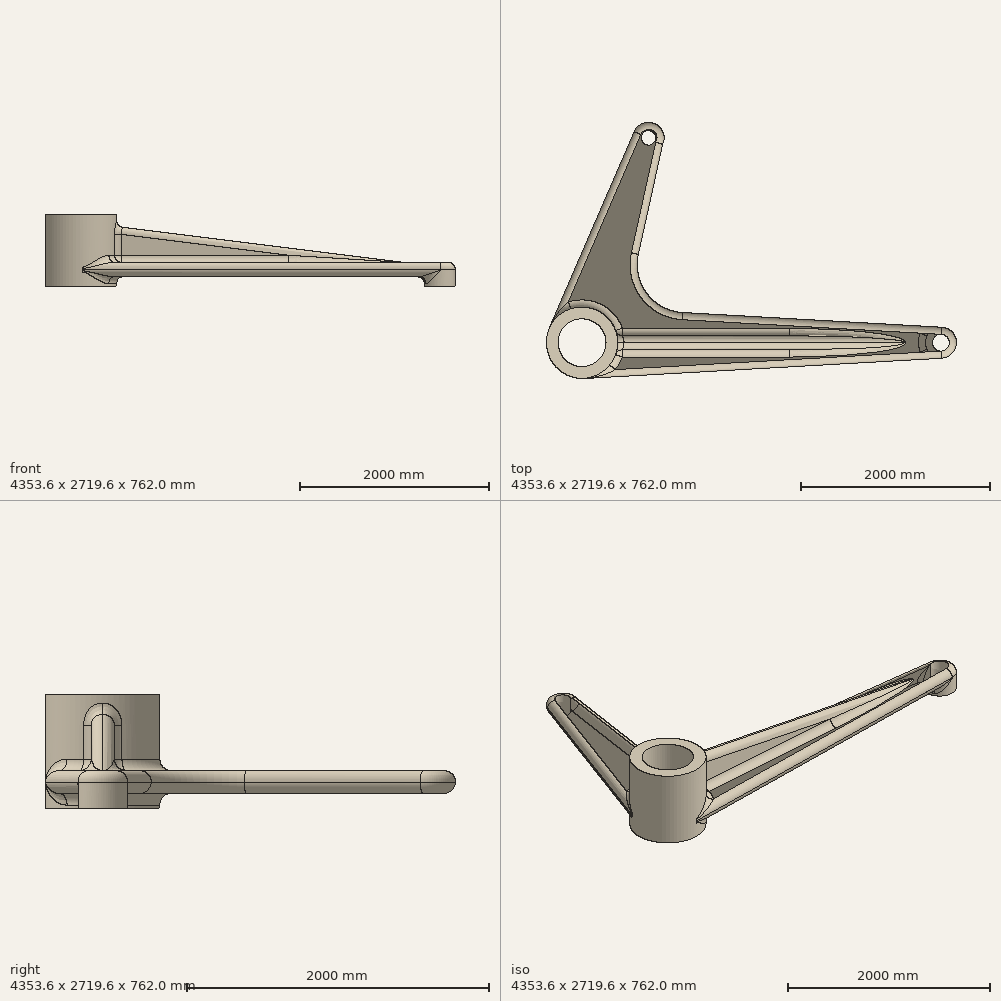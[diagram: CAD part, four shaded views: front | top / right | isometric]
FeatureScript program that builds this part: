
annotation { "Feature Type Name" : "Feature", "Feature Type Description" : "" }
export const myFeature = defineFeature(function(context is Context, id is Id, definition is map)
    precondition{}
    {
        {
            var Q0;
            Q0=qCreatedBy(makeId("Top.planeOp"),FACE);
            var sketch = newSketch(context, id + "F0", { "sketchPlane" : qUnion([Q0])});
            skArc(sketch, "E0", {"start": v(21.59, 380.39) * mm, "mid": v(-381, 0) * mm, "end": v(21.59, -380.39) * mm});
            skArc(sketch, "E1", {"start": v(3819.36, -164.83) * mm, "mid": v(3975.1, 0) * mm, "end": v(3819.36, 164.83) * mm});
            skLineSegment(sketch, "E2", {"start": v(3819.36, 164.83) * mm, "end": v(21.59, 380.39) * mm});
            skLineSegment(sketch, "E3", {"start": v(3819.36, -164.83) * mm, "end": v(21.59, -380.39) * mm});
            skSolve(sketch);
        }
        {
            var Q0;
            Q0 = qSketchRegion(id + "F0", true);
            extrude(context, id + "F1", {"entities" : qUnion([Q0]), "oppositeDirection" : true, "depth" : 152.4 * mm, "offsetDistance" : 25.4 * mm});
        }
        {
            var Q0;
            Q0=makeQuery(id+"F1.opExtrude","CAP_FACE",FACE,{"disambiguationData":[OSD([sQuery(id+"F0.wireOp",EDGE,"E0"),sQuery(id+"F0.wireOp",EDGE,"E1"),sQuery(id+"F0.wireOp",EDGE,"E2"),sQuery(id+"F0.wireOp",EDGE,"E3")])],"isStart":true});
            var sketch = newSketch(context, id + "F2", { "sketchPlane" : qUnion([Q0])});
            skLineSegment(sketch, "E4", {"start": v(0, 0) * mm, "end": v(706.41, 2174.12) * mm, "construction": true});
            skLineSegment(sketch, "E5", {"start": v(0, 0) * mm, "end": v(5447.22, 0) * mm, "construction": true});
            skArc(sketch, "E6", {"start": v(856.09, 2104.43) * mm, "mid": v(774.07, 2324.72) * mm, "end": v(554.91, 2239.74) * mm});
            skArc(sketch, "E7", {"start": v(-349.61, 151.43) * mm, "mid": v(-77.32, -373.07) * mm, "end": v(381, 0) * mm});
            skLineSegment(sketch, "E8", {"start": v(554.91, 2239.74) * mm, "end": v(-349.61, 151.43) * mm});
            skLineSegment(sketch, "E9", {"start": v(871.51, 2174.12) * mm, "end": v(372, -82.35) * mm});
            skCircle(sketch, "E10", {"center": v(706.41, 2174.12) * mm, "radius": 76.2 * mm});
            skSolve(sketch);
        }
        {
            var Q0;
            Q0 = qSketchRegion(id + "F2", true);
            extrude(context, id + "F3", {"entities" : qUnion([Q0]), "operationType" : NewBodyOperationType.ADD, "oppositeDirection" : true, "depth" : 152.4 * mm, "offsetDistance" : 25.4 * mm});
        }
        {
            var Q0;
            Q0=makeQuery(id+"F3.boolean.opBoolean","INTERSECT",EDGE,{"derivedFrom":[makeQuery(id+"F1.opExtrude","SWEPT_FACE",FACE,{"disambiguationData":[OSD([sQuery(id+"F0.wireOp",EDGE,"E2")])]}),makeQuery(id+"F3.opExtrude","SWEPT_FACE",FACE,{"disambiguationData":[OSD([sQuery(id+"F2.wireOp",EDGE,"E9")])]})]});
            fillet(context, id + "F4", {"entities" : qUnion([Q0]), "radius" : 508 * mm, "tangentPropagation" : true, "allowEdgeOverflow" : false});
        }
        {
            var Q0;
            Q0=makeQuery(id+"F3.boolean.opBoolean","MERGE",FACE,{"derivedFrom":[makeQuery(id+"F1.opExtrude","CAP_FACE",FACE,{"disambiguationData":[OSD([sQuery(id+"F0.wireOp",EDGE,"E0"),sQuery(id+"F0.wireOp",EDGE,"E1"),sQuery(id+"F0.wireOp",EDGE,"E2"),sQuery(id+"F0.wireOp",EDGE,"E3")])],"isStart":true}),makeQuery(id+"F3.opExtrude","CAP_FACE",FACE,{"disambiguationData":[OSD([sQuery(id+"F2.wireOp",EDGE,"E6"),sQuery(id+"F2.wireOp",EDGE,"E7"),sQuery(id+"F2.wireOp",EDGE,"E8"),sQuery(id+"F2.wireOp",EDGE,"E9"),sQuery(id+"F2.wireOp",EDGE,"E10")])],"isStart":true})]});
            var sketch = newSketch(context, id + "F5", { "sketchPlane" : qUnion([Q0])});
            skArc(sketch, "E11.0", {"start": v(-349.61, 151.43) * mm, "mid": v(-312.42, -218.07) * mm, "end": v(21.59, -380.39) * mm});
            skLineSegment(sketch, "E12", {"start": v(171.2, -594.74) * mm, "end": v(-512.95, 385.44) * mm});
            skLineSegment(sketch, "E13", {"start": v(-512.95, 385.44) * mm, "end": v(-727.28, 151.43) * mm});
            skLineSegment(sketch, "E14", {"start": v(-727.28, 151.43) * mm, "end": v(-179.02, -822.73) * mm});
            skLineSegment(sketch, "E15", {"start": v(-179.02, -822.73) * mm, "end": v(171.2, -594.74) * mm});
            skSolve(sketch);
        }
        {
            var Q0;
            Q0 = qSketchRegion(id + "F5", true);
            extrude(context, id + "F6", {"entities" : qUnion([Q0]), "operationType" : NewBodyOperationType.REMOVE, "endBound" : BoundingType.THROUGH_ALL, "oppositeDirection" : true, "depth" : 25.4 * mm, "offsetDistance" : 25.4 * mm});
        }
        {
            var Q0;
            {var subQ0=sQuery(id+"F2.wireOp",EDGE,"E9");var subQ1=sQuery(id+"F0.wireOp",EDGE,"E2");Q0=makeQuery(id+"F4.opFillet","BLEND_EDGE",EDGE,{"blendedFrom":[makeQuery(id+"F3.boolean.opBoolean","INTERSECT",EDGE,{"derivedFrom":[makeQuery(id+"F1.opExtrude","SWEPT_FACE",FACE,{"disambiguationData":[OSD([subQ1])]}),makeQuery(id+"F3.opExtrude","SWEPT_FACE",FACE,{"disambiguationData":[OSD([subQ0])]})]}),makeQuery(id+"F3.boolean.opBoolean","MERGE",FACE,{"derivedFrom":[makeQuery(id+"F1.opExtrude","CAP_FACE",FACE,{"disambiguationData":[OSD([sQuery(id+"F0.wireOp",EDGE,"E0"),sQuery(id+"F0.wireOp",EDGE,"E1"),subQ1,sQuery(id+"F0.wireOp",EDGE,"E3")])],"isStart":true}),makeQuery(id+"F3.opExtrude","CAP_FACE",FACE,{"disambiguationData":[OSD([sQuery(id+"F2.wireOp",EDGE,"E6"),sQuery(id+"F2.wireOp",EDGE,"E7"),sQuery(id+"F2.wireOp",EDGE,"E8"),subQ0,sQuery(id+"F2.wireOp",EDGE,"E10")])],"isStart":true})]})],"blendedInto":[makeQuery(id+"F3.boolean.opBoolean","MERGE",FACE,{"derivedFrom":[makeQuery(id+"F1.opExtrude","CAP_FACE",FACE,{"disambiguationData":[OSD([sQuery(id+"F0.wireOp",EDGE,"E0"),sQuery(id+"F0.wireOp",EDGE,"E1"),subQ1,sQuery(id+"F0.wireOp",EDGE,"E3")])],"isStart":true}),makeQuery(id+"F3.opExtrude","CAP_FACE",FACE,{"disambiguationData":[OSD([sQuery(id+"F2.wireOp",EDGE,"E6"),sQuery(id+"F2.wireOp",EDGE,"E7"),sQuery(id+"F2.wireOp",EDGE,"E8"),subQ0,sQuery(id+"F2.wireOp",EDGE,"E10")])],"isStart":true})]})]});}
            fillet(context, id + "F7", {"entities" : qUnion([Q0]), "radius" : 76.17 * mm, "tangentPropagation" : true, "allowEdgeOverflow" : false});
        }
        {
            var Q0;
            Q0=makeQuery(id+"F3.opExtrude","CAP_EDGE",EDGE,{"disambiguationData":[OSD([sQuery(id+"F2.wireOp",EDGE,"E6")])],"isStart":true});
            fillet(context, id + "F8", {"entities" : qUnion([Q0]), "radius" : 76.17 * mm, "tangentPropagation" : true, "allowEdgeOverflow" : false});
        }
        {
            var Q0;
            {var subQ0=sQuery(id+"F2.wireOp",EDGE,"E9");var subQ1=sQuery(id+"F0.wireOp",EDGE,"E2");Q0=makeQuery(id+"F4.opFillet","BLEND_EDGE",EDGE,{"blendedFrom":[makeQuery(id+"F3.boolean.opBoolean","INTERSECT",EDGE,{"derivedFrom":[makeQuery(id+"F1.opExtrude","SWEPT_FACE",FACE,{"disambiguationData":[OSD([subQ1])]}),makeQuery(id+"F3.opExtrude","SWEPT_FACE",FACE,{"disambiguationData":[OSD([subQ0])]})]}),makeQuery(id+"F3.boolean.opBoolean","MERGE",FACE,{"derivedFrom":[makeQuery(id+"F1.opExtrude","CAP_FACE",FACE,{"disambiguationData":[OSD([sQuery(id+"F0.wireOp",EDGE,"E0"),sQuery(id+"F0.wireOp",EDGE,"E1"),subQ1,sQuery(id+"F0.wireOp",EDGE,"E3")])],"isStart":false}),makeQuery(id+"F3.opExtrude","CAP_FACE",FACE,{"disambiguationData":[OSD([sQuery(id+"F2.wireOp",EDGE,"E6"),sQuery(id+"F2.wireOp",EDGE,"E7"),sQuery(id+"F2.wireOp",EDGE,"E8"),subQ0,sQuery(id+"F2.wireOp",EDGE,"E10")])],"isStart":false})]})],"blendedInto":[makeQuery(id+"F3.boolean.opBoolean","MERGE",FACE,{"derivedFrom":[makeQuery(id+"F1.opExtrude","CAP_FACE",FACE,{"disambiguationData":[OSD([sQuery(id+"F0.wireOp",EDGE,"E0"),sQuery(id+"F0.wireOp",EDGE,"E1"),subQ1,sQuery(id+"F0.wireOp",EDGE,"E3")])],"isStart":false}),makeQuery(id+"F3.opExtrude","CAP_FACE",FACE,{"disambiguationData":[OSD([sQuery(id+"F2.wireOp",EDGE,"E6"),sQuery(id+"F2.wireOp",EDGE,"E7"),sQuery(id+"F2.wireOp",EDGE,"E8"),subQ0,sQuery(id+"F2.wireOp",EDGE,"E10")])],"isStart":false})]})]});}
            fillet(context, id + "F9", {"entities" : qUnion([Q0]), "radius" : 76.17 * mm, "tangentPropagation" : true, "allowEdgeOverflow" : false});
        }
        {
            var Q0;
            Q0=makeQuery(id+"F3.opExtrude","CAP_EDGE",EDGE,{"disambiguationData":[OSD([sQuery(id+"F2.wireOp",EDGE,"E6")])],"isStart":false});
            fillet(context, id + "F10", {"entities" : qUnion([Q0]), "radius" : 76.17 * mm, "tangentPropagation" : true, "allowEdgeOverflow" : false});
        }
        {
            var Q0;
            Q0=makeQuery(id+"F3.boolean.opBoolean","MERGE",FACE,{"derivedFrom":[makeQuery(id+"F1.opExtrude","CAP_FACE",FACE,{"disambiguationData":[OSD([sQuery(id+"F0.wireOp",EDGE,"E0"),sQuery(id+"F0.wireOp",EDGE,"E1"),sQuery(id+"F0.wireOp",EDGE,"E2"),sQuery(id+"F0.wireOp",EDGE,"E3")])],"isStart":false}),makeQuery(id+"F3.opExtrude","CAP_FACE",FACE,{"disambiguationData":[OSD([sQuery(id+"F2.wireOp",EDGE,"E6"),sQuery(id+"F2.wireOp",EDGE,"E7"),sQuery(id+"F2.wireOp",EDGE,"E8"),sQuery(id+"F2.wireOp",EDGE,"E9"),sQuery(id+"F2.wireOp",EDGE,"E10")])],"isStart":false})]});
            var sketch = newSketch(context, id + "F11", { "sketchPlane" : qUnion([Q0])});
            skArc(sketch, "E16.0", {"start": v(3819.36, 164.83) * mm, "mid": v(3975.1, 0) * mm, "end": v(3819.36, -164.83) * mm});
            skLineSegment(sketch, "E17.bottom", {"start": v(4003.68, 216.65) * mm, "end": v(3819.36, 216.65) * mm});
            skLineSegment(sketch, "E17.top", {"start": v(4003.68, -288.23) * mm, "end": v(3819.36, -288.23) * mm});
            skLineSegment(sketch, "E17.left", {"start": v(4003.68, 216.65) * mm, "end": v(4003.68, -288.23) * mm});
            skLineSegment(sketch, "E17.right", {"start": v(3819.36, 216.65) * mm, "end": v(3819.36, -288.23) * mm});
            skSolve(sketch);
        }
        {
            var Q0;
            Q0 = qSketchRegion(id + "F11", true);
            extrude(context, id + "F12", {"entities" : qUnion([Q0]), "operationType" : NewBodyOperationType.REMOVE, "oppositeDirection" : true, "depth" : 76.2 * mm, "offsetDistance" : 25.4 * mm});
        }
        {
            var Q0;
            Q0=makeQuery(id+"F12.boolean.opBoolean","COPY",FACE,{"derivedFrom":makeQuery(id+"F12.opExtrude","CAP_FACE",FACE,{"disambiguationData":[OSD([sQuery(id+"F11.wireOp",EDGE,"E17.bottom"),sQuery(id+"F11.wireOp",EDGE,"E17.top"),sQuery(id+"F11.wireOp",EDGE,"E17.left"),sQuery(id+"F11.wireOp",EDGE,"E17.right")])],"isStart":false})});
            var sketch = newSketch(context, id + "F13", { "sketchPlane" : qUnion([Q0])});
            skArc(sketch, "E18.0", {"start": v(3819.36, 164.83) * mm, "mid": v(3975.1, 0) * mm, "end": v(3819.36, -164.83) * mm});
            skCircle(sketch, "E19", {"center": v(3810, 0) * mm, "radius": 163.83 * mm});
            skSolve(sketch);
        }
        {
            var Q0;
            Q0 = qSketchRegion(id + "F13", true);
            extrude(context, id + "F14", {"entities" : qUnion([Q0]), "operationType" : NewBodyOperationType.ADD, "depth" : 177.8 * mm, "offsetDistance" : 25.4 * mm});
        }
        {
            var Q0;
            Q0=makeQuery(id+"F14.boolean.opBoolean","INTERSECT",EDGE,{"derivedFrom":[makeQuery(id+"F3.boolean.opBoolean","MERGE",FACE,{"derivedFrom":[makeQuery(id+"F1.opExtrude","CAP_FACE",FACE,{"disambiguationData":[OSD([sQuery(id+"F0.wireOp",EDGE,"E0"),sQuery(id+"F0.wireOp",EDGE,"E1"),sQuery(id+"F0.wireOp",EDGE,"E2"),sQuery(id+"F0.wireOp",EDGE,"E3")])],"isStart":false}),makeQuery(id+"F3.opExtrude","CAP_FACE",FACE,{"disambiguationData":[OSD([sQuery(id+"F2.wireOp",EDGE,"E6"),sQuery(id+"F2.wireOp",EDGE,"E7"),sQuery(id+"F2.wireOp",EDGE,"E8"),sQuery(id+"F2.wireOp",EDGE,"E9"),sQuery(id+"F2.wireOp",EDGE,"E10")])],"isStart":false})]}),makeQuery(id+"F14.opExtrude","SWEPT_FACE",FACE,{"disambiguationData":[OSD([sQuery(id+"F13.wireOp",EDGE,"E19")])]})]});
            fillet(context, id + "F15", {"entities" : qUnion([Q0]), "radius" : 76.2 * mm, "tangentPropagation" : true, "allowEdgeOverflow" : false});
        }
        {
            var Q0;
            Q0=makeQuery(id+"F3.boolean.opBoolean","MERGE",FACE,{"derivedFrom":[makeQuery(id+"F1.opExtrude","CAP_FACE",FACE,{"disambiguationData":[OSD([sQuery(id+"F0.wireOp",EDGE,"E0"),sQuery(id+"F0.wireOp",EDGE,"E1"),sQuery(id+"F0.wireOp",EDGE,"E2"),sQuery(id+"F0.wireOp",EDGE,"E3")])],"isStart":true}),makeQuery(id+"F3.opExtrude","CAP_FACE",FACE,{"disambiguationData":[OSD([sQuery(id+"F2.wireOp",EDGE,"E6"),sQuery(id+"F2.wireOp",EDGE,"E7"),sQuery(id+"F2.wireOp",EDGE,"E8"),sQuery(id+"F2.wireOp",EDGE,"E9"),sQuery(id+"F2.wireOp",EDGE,"E10")])],"isStart":true})]});
            var sketch = newSketch(context, id + "F16", { "sketchPlane" : qUnion([Q0])});
            skCircle(sketch, "E20", {"center": v(0, 0) * mm, "radius": 378.46 * mm});
            skSolve(sketch);
        }
        {
            var Q0;
            Q0 = qSketchRegion(id + "F16", true);
            extrude(context, id + "F17", {"entities" : qUnion([Q0]), "operationType" : NewBodyOperationType.ADD, "depth" : 508 * mm, "offsetDistance" : 25.4 * mm, "hasSecondDirection" : true, "secondDirectionOppositeDirection" : true, "secondDirectionDepth" : 254 * mm});
        }
        {
            var Q0;
            Q0=makeQuery(id+"F17.boolean.opBoolean","INTERSECT",EDGE,{"derivedFrom":[makeQuery(id+"F3.boolean.opBoolean","MERGE",FACE,{"derivedFrom":[makeQuery(id+"F1.opExtrude","CAP_FACE",FACE,{"disambiguationData":[OSD([sQuery(id+"F0.wireOp",EDGE,"E0"),sQuery(id+"F0.wireOp",EDGE,"E1"),sQuery(id+"F0.wireOp",EDGE,"E2"),sQuery(id+"F0.wireOp",EDGE,"E3")])],"isStart":true}),makeQuery(id+"F3.opExtrude","CAP_FACE",FACE,{"disambiguationData":[OSD([sQuery(id+"F2.wireOp",EDGE,"E6"),sQuery(id+"F2.wireOp",EDGE,"E7"),sQuery(id+"F2.wireOp",EDGE,"E8"),sQuery(id+"F2.wireOp",EDGE,"E9"),sQuery(id+"F2.wireOp",EDGE,"E10")])],"isStart":true})]}),makeQuery(id+"F17.opExtrude","SWEPT_FACE",FACE,{"disambiguationData":[OSD([sQuery(id+"F16.wireOp",EDGE,"E20")])]})]});
            fillet(context, id + "F18", {"entities" : qUnion([Q0]), "radius" : 76.2 * mm, "tangentPropagation" : true, "allowEdgeOverflow" : false});
        }
        {
            var Q0;
            Q0=makeQuery(id+"F17.boolean.opBoolean","INTERSECT",EDGE,{"derivedFrom":[makeQuery(id+"F3.boolean.opBoolean","MERGE",FACE,{"derivedFrom":[makeQuery(id+"F1.opExtrude","CAP_FACE",FACE,{"disambiguationData":[OSD([sQuery(id+"F0.wireOp",EDGE,"E0"),sQuery(id+"F0.wireOp",EDGE,"E1"),sQuery(id+"F0.wireOp",EDGE,"E2"),sQuery(id+"F0.wireOp",EDGE,"E3")])],"isStart":false}),makeQuery(id+"F3.opExtrude","CAP_FACE",FACE,{"disambiguationData":[OSD([sQuery(id+"F2.wireOp",EDGE,"E6"),sQuery(id+"F2.wireOp",EDGE,"E7"),sQuery(id+"F2.wireOp",EDGE,"E8"),sQuery(id+"F2.wireOp",EDGE,"E9"),sQuery(id+"F2.wireOp",EDGE,"E10")])],"isStart":false})]}),makeQuery(id+"F17.opExtrude","SWEPT_FACE",FACE,{"disambiguationData":[OSD([sQuery(id+"F16.wireOp",EDGE,"E20")])]})]});
            fillet(context, id + "F19", {"entities" : qUnion([Q0]), "radius" : 76.2 * mm, "tangentPropagation" : true, "allowEdgeOverflow" : false});
        }
        {
            var Q0;
            Q0=qCreatedBy(makeId("Front.planeOp"),FACE);
            var sketch = newSketch(context, id + "F20", { "sketchPlane" : qUnion([Q0])});
            skLineSegment(sketch, "E21", {"start": v(204.35, 403.08) * mm, "end": v(204.35, 0) * mm});
            skLineSegment(sketch, "E22", {"start": v(204.35, 0) * mm, "end": v(3429, 0) * mm});
            skLineSegment(sketch, "E23", {"start": v(3429, 0) * mm, "end": v(204.35, 403.08) * mm});
            skLineSegment(sketch, "E24", {"start": v(381, 381) * mm, "end": v(381, 0) * mm, "construction": true});
            skLineSegment(sketch, "E25", {"start": v(0, 0) * mm, "end": v(-607.64, 0) * mm, "construction": true});
            skSolve(sketch);
        }
        {
            var Q0;
            Q0 = qSketchRegion(id + "F20", true);
            extrude(context, id + "F21", {"entities" : qUnion([Q0]), "operationType" : NewBodyOperationType.ADD, "endBound" : BoundingType.SYMMETRIC, "depth" : 152.4 * mm, "offsetDistance" : 25.4 * mm});
        }
        {
            var Q0;
            Q0=makeQuery(id+"F21.opExtrude","CAP_EDGE",EDGE,{"disambiguationData":[OSD([sQuery(id+"F20.wireOp",EDGE,"E23")])],"isStart":false});
            var Q1;
            Q1=makeQuery(id+"F21.opExtrude","CAP_EDGE",EDGE,{"disambiguationData":[OSD([sQuery(id+"F20.wireOp",EDGE,"E23")])],"isStart":true});
            fillet(context, id + "F22", {"entities" : qUnion([Q0, Q1]), "radius" : 76.17 * mm, "tangentPropagation" : true, "allowEdgeOverflow" : false});
        }
        {
            var Q0;
            Q0=makeQuery(id+"F22.opFillet","BLEND_EDGE",EDGE,{"blendedFrom":[makeQuery(id+"F21.opExtrude","CAP_EDGE",EDGE,{"disambiguationData":[OSD([sQuery(id+"F20.wireOp",EDGE,"E23")])],"isStart":false}),makeQuery(id+"F17.opExtrude","SWEPT_FACE",FACE,{"disambiguationData":[OSD([sQuery(id+"F16.wireOp",EDGE,"E20")])]})],"blendedInto":[makeQuery(id+"F17.opExtrude","SWEPT_FACE",FACE,{"disambiguationData":[OSD([sQuery(id+"F16.wireOp",EDGE,"E20")])]})]});
            fillet(context, id + "F23", {"entities" : qUnion([Q0]), "radius" : 76.2 * mm, "tangentPropagation" : true, "allowEdgeOverflow" : false});
        }
        {
            var Q0;
            Q0=makeQuery(id+"F17.opExtrude","CAP_FACE",FACE,{"disambiguationData":[OSD([sQuery(id+"F16.wireOp",EDGE,"E20")])],"isStart":false});
            var sketch = newSketch(context, id + "F24", { "sketchPlane" : qUnion([Q0])});
            skCircle(sketch, "E26", {"center": v(0, 0) * mm, "radius": 254 * mm});
            skSolve(sketch);
        }
        {
            var Q0;
            Q0 = qSketchRegion(id + "F24", true);
            extrude(context, id + "F25", {"entities" : qUnion([Q0]), "operationType" : NewBodyOperationType.REMOVE, "endBound" : BoundingType.THROUGH_ALL, "oppositeDirection" : true, "depth" : 25.4 * mm, "offsetDistance" : 25.4 * mm});
        }
        {
            var Q0;
            Q0=makeQuery(id+"F14.opExtrude","CAP_FACE",FACE,{"disambiguationData":[OSD([sQuery(id+"F13.wireOp",EDGE,"E19")])],"isStart":false});
            var sketch = newSketch(context, id + "F26", { "sketchPlane" : qUnion([Q0])});
            skCircle(sketch, "E27", {"center": v(3810, 0) * mm, "radius": 88.9 * mm});
            skSolve(sketch);
        }
        {
            var Q0;
            Q0=makeQuery(id+"F26.imprint","IMPRINT",FACE,{"disambiguationData":[TD([[makeQuery(id+"F26.imprint","IMPRINT",EDGE,{"derivedFrom":sQuery(id+"F26.wireOp",EDGE,"E27")}),1.0]])]});
            extrude(context, id + "F27", {"entities" : qUnion([Q0]), "operationType" : NewBodyOperationType.REMOVE, "endBound" : BoundingType.THROUGH_ALL, "oppositeDirection" : true, "depth" : 25.4 * mm, "offsetDistance" : 25.4 * mm});
        }
    });
